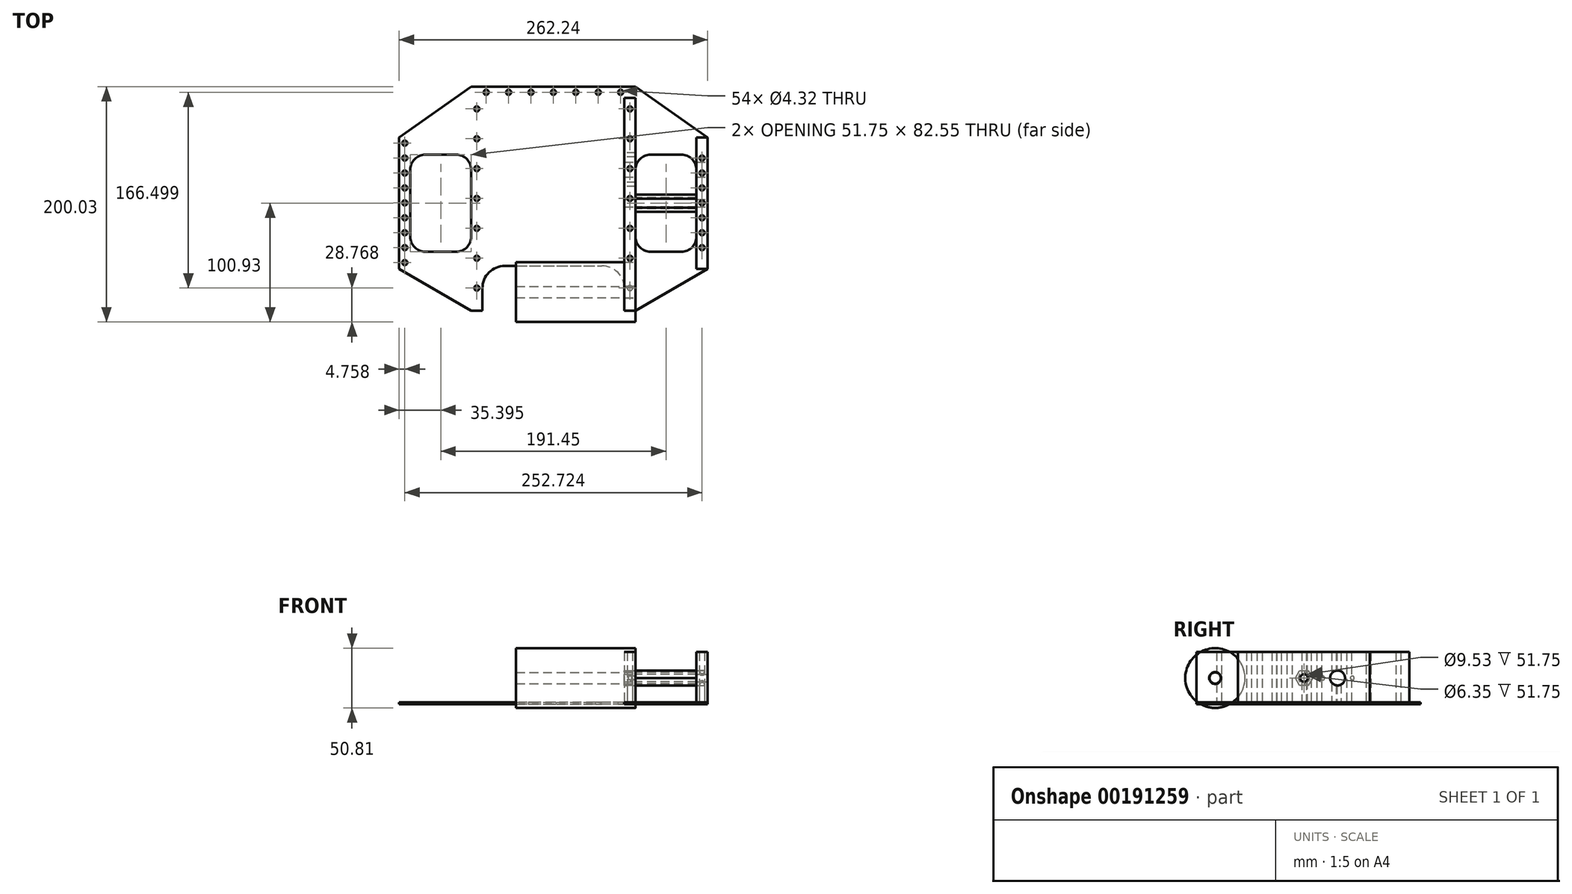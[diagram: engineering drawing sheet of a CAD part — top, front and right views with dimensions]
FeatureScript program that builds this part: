
annotation { "Feature Type Name" : "Feature", "Feature Type Description" : "" }
export const myFeature = defineFeature(function(context is Context, id is Id, definition is map)
    precondition{}
    {
        {
            var Q0;
            Q0=qCreatedBy(makeId("Top.planeOp"),FACE);
            var sketch = newSketch(context, id + "F0", { "sketchPlane" : qUnion([Q0])});
            skLineSegment(sketch, "E0.bottom", {"start": v(82.55, 31.75) * mm, "end": v(114.3, 31.75) * mm});
            skLineSegment(sketch, "E0.top", {"start": v(82.55, -31.75) * mm, "end": v(114.3, -31.75) * mm});
            skLineSegment(sketch, "E0.left", {"start": v(82.55, 31.75) * mm, "end": v(82.55, -31.75) * mm});
            skLineSegment(sketch, "E0.right", {"start": v(114.3, 31.75) * mm, "end": v(114.3, -31.75) * mm});
            skPoint(sketch, "E0.middle", {"position": v(98.43, 0) * mm});
            skLineSegment(sketch, "E1.bottom", {"start": v(48.7, -59.65) * mm, "end": v(-48.7, -59.65) * mm, "construction": true});
            skLineSegment(sketch, "E1.left", {"start": v(48.7, -59.65) * mm, "end": v(48.7, -91.4) * mm, "construction": true});
            skLineSegment(sketch, "E1.right", {"start": v(-48.7, -59.65) * mm, "end": v(-48.7, -91.4) * mm, "construction": true});
            skPoint(sketch, "E1.middle", {"position": v(0, -75.53) * mm});
            skLineSegment(sketch, "E2", {"start": v(0, 0) * mm, "end": v(0, 61.83) * mm, "construction": true});
            skLineSegment(sketch, "E3.MirrorCS", {"start": v(-82.55, 31.75) * mm, "end": v(-114.3, 31.75) * mm});
            skLineSegment(sketch, "E4.MirrorCS", {"start": v(-82.55, -31.75) * mm, "end": v(-114.3, -31.75) * mm});
            skLineSegment(sketch, "E5.MirrorCS", {"start": v(-82.55, 31.75) * mm, "end": v(-82.55, -31.75) * mm});
            skLineSegment(sketch, "E6.MirrorCS", {"start": v(-114.3, 31.75) * mm, "end": v(-114.3, -31.75) * mm});
            skPoint(sketch, "E7.MirrorP", {"position": v(-98.43, 0) * mm});
            skLineSegment(sketch, "E8.bottom", {"start": v(69.85, 89.57) * mm, "end": v(0, 89.57) * mm});
            skLineSegment(sketch, "E8.top", {"start": v(69.85, 99.1) * mm, "end": v(0, 99.1) * mm});
            skPoint(sketch, "E9.middle", {"position": v(80.32, 28.57) * mm});
            skLineSegment(sketch, "E10.bottom", {"start": v(60.33, 7.57) * mm, "end": v(10.32, 7.57) * mm});
            skLineSegment(sketch, "E10.top", {"start": v(60.33, 49.57) * mm, "end": v(10.32, 49.57) * mm});
            skLineSegment(sketch, "E10.left", {"start": v(60.33, 7.57) * mm, "end": v(60.33, 49.57) * mm});
            skLineSegment(sketch, "E10.right", {"start": v(10.32, 7.57) * mm, "end": v(10.32, 49.57) * mm});
            skPoint(sketch, "E10.middle", {"position": v(35.33, 28.57) * mm});
            skLineSegment(sketch, "E11.bottom", {"start": v(60.33, 89.57) * mm, "end": v(69.85, 89.57) * mm});
            skLineSegment(sketch, "E11.top", {"start": v(60.33, -91.4) * mm, "end": v(69.85, -91.4) * mm});
            skLineSegment(sketch, "E11.left", {"start": v(60.33, 89.57) * mm, "end": v(60.33, -91.4) * mm});
            skLineSegment(sketch, "E11.right", {"start": v(69.85, 89.57) * mm, "end": v(69.85, -91.4) * mm});
            skLineSegment(sketch, "E12.bottom", {"start": v(60.33, 31.07) * mm, "end": v(80.32, 31.07) * mm});
            skLineSegment(sketch, "E12.top", {"start": v(60.33, 26.07) * mm, "end": v(80.32, 26.07) * mm});
            skLineSegment(sketch, "E12.left", {"start": v(60.33, 31.07) * mm, "end": v(60.33, 26.07) * mm});
            skLineSegment(sketch, "E12.right", {"start": v(80.32, 31.07) * mm, "end": v(80.32, 26.07) * mm});
            skLineSegment(sketch, "E13.bottom", {"start": v(73.03, 23.81) * mm, "end": v(82.55, 23.81) * mm});
            skLineSegment(sketch, "E13.top", {"start": v(73.03, -23.81) * mm, "end": v(82.55, -23.81) * mm});
            skLineSegment(sketch, "E13.left", {"start": v(73.03, 23.81) * mm, "end": v(73.03, -23.81) * mm});
            skLineSegment(sketch, "E13.right", {"start": v(82.55, 23.81) * mm, "end": v(82.55, -23.81) * mm});
            skPoint(sketch, "E13.middle", {"position": v(77.79, 0) * mm});
            skLineSegment(sketch, "E14.bottom", {"start": v(80.32, 33.34) * mm, "end": v(67.62, 33.34) * mm});
            skLineSegment(sketch, "E14.top", {"start": v(80.32, 23.81) * mm, "end": v(67.62, 23.81) * mm});
            skLineSegment(sketch, "E14.left", {"start": v(80.32, 33.34) * mm, "end": v(80.32, 23.81) * mm});
            skLineSegment(sketch, "E14.right", {"start": v(67.62, 33.34) * mm, "end": v(67.62, 23.81) * mm});
            skPoint(sketch, "E14.middle", {"position": v(73.97, 28.57) * mm});
            skLineSegment(sketch, "E15", {"start": v(69.85, 99.1) * mm, "end": v(69.85, 89.57) * mm});
            skLineSegment(sketch, "E16", {"start": v(69.85, 99.1) * mm, "end": v(131.12, 56.02) * mm});
            skLineSegment(sketch, "E17.trimOffspring", {"start": v(131.12, 56.02) * mm, "end": v(131.12, -56.02) * mm});
            skLineSegment(sketch, "E18", {"start": v(131.12, -56.02) * mm, "end": v(69.85, -91.4) * mm});
            skPoint(sketch, "E19", {"position": v(131.12, 0) * mm});
            skLineSegment(sketch, "E20.0", {"start": v(121.6, -50.52) * mm, "end": v(69.85, -80.4) * mm, "construction": true});
            skLineSegment(sketch, "E20.1", {"start": v(121.6, 51.08) * mm, "end": v(121.6, -50.52) * mm, "construction": true});
            skLineSegment(sketch, "E21.trimOffspring", {"start": v(69.85, 87.46) * mm, "end": v(121.6, 51.08) * mm, "construction": true});
            skLineSegment(sketch, "E22.bottom", {"start": v(51.38, -53.06) * mm, "end": v(30.38, -53.06) * mm});
            skLineSegment(sketch, "E22.top", {"start": v(51.38, -3.06) * mm, "end": v(30.38, -3.06) * mm});
            skLineSegment(sketch, "E22.left", {"start": v(51.38, -53.06) * mm, "end": v(51.38, -3.06) * mm});
            skLineSegment(sketch, "E22.right", {"start": v(30.38, -53.06) * mm, "end": v(30.38, -3.06) * mm});
            skPoint(sketch, "E22.middle", {"position": v(40.88, -28.06) * mm});
            skSolve(sketch);
        }
        {
            var Q0;
            Q0=qCreatedBy(makeId("Top.planeOp"),FACE);
            var sketch = newSketch(context, id + "F1", { "sketchPlane" : qUnion([Q0])});
            skLineSegment(sketch, "E23.0", {"start": v(69.85, 99.1) * mm, "end": v(0, 99.1) * mm});
            skLineSegment(sketch, "E23.1", {"start": v(69.85, 99.1) * mm, "end": v(131.12, 56.02) * mm});
            skLineSegment(sketch, "E23.2", {"start": v(131.12, 56.02) * mm, "end": v(131.12, -56.02) * mm});
            skLineSegment(sketch, "E23.3", {"start": v(131.12, -56.02) * mm, "end": v(69.85, -91.4) * mm});
            skLineSegment(sketch, "E23.4", {"start": v(60.33, -91.4) * mm, "end": v(69.85, -91.4) * mm});
            skLineSegment(sketch, "E23.5", {"start": v(60.33, -53.3) * mm, "end": v(60.33, -91.4) * mm});
            skLineSegment(sketch, "E24", {"start": v(60.33, -53.3) * mm, "end": v(0, -53.3) * mm});
            skPoint(sketch, "E25.orphan", {"position": v(60.33, 89.57) * mm});
            skLineSegment(sketch, "E26.0", {"start": v(0, 0) * mm, "end": v(0, 61.83) * mm, "construction": true});
            skLineSegment(sketch, "E27.MirrorCS", {"start": v(-69.85, 99.1) * mm, "end": v(0, 99.1) * mm});
            skLineSegment(sketch, "E28.MirrorCS", {"start": v(-69.85, 99.1) * mm, "end": v(-131.12, 56.02) * mm});
            skLineSegment(sketch, "E29.MirrorCS", {"start": v(-60.33, -53.3) * mm, "end": v(0, -53.3) * mm});
            skPoint(sketch, "E30.MirrorP", {"position": v(-60.33, 89.57) * mm});
            skLineSegment(sketch, "E31.MirrorCS", {"start": v(-60.33, -53.3) * mm, "end": v(-60.33, -91.4) * mm});
            skLineSegment(sketch, "E32.MirrorCS", {"start": v(-60.33, -91.4) * mm, "end": v(-69.85, -91.4) * mm});
            skLineSegment(sketch, "E33.MirrorCS", {"start": v(-131.12, 56.02) * mm, "end": v(-131.12, -56.02) * mm});
            skLineSegment(sketch, "E34.MirrorCS", {"start": v(-131.12, -56.02) * mm, "end": v(-69.85, -91.4) * mm});
            skSolve(sketch);
        }
        {
            var Q0;
            Q0=qCreatedBy(makeId("Top.planeOp"),FACE);
            var sketch = newSketch(context, id + "F2", { "sketchPlane" : qUnion([Q0])});
            skPoint(sketch, "E35.0", {"position": v(65.09, 89.57) * mm});
            skPoint(sketch, "E35.1", {"position": v(65.09, -91.4) * mm});
            skPoint(sketch, "E36.0", {"position": v(121.6, 51.08) * mm});
            skPoint(sketch, "E36.1", {"position": v(121.6, -50.52) * mm});
            skLineSegment(sketch, "E37", {"start": v(65.09, 89.57) * mm, "end": v(65.09, -91.4) * mm, "construction": true});
            skLineSegment(sketch, "E38.0", {"start": v(131.12, 56.02) * mm, "end": v(131.12, -56.02) * mm, "construction": true});
            skLineSegment(sketch, "E39", {"start": v(121.6, 51.08) * mm, "end": v(131.12, 51.08) * mm, "construction": true});
            skLineSegment(sketch, "E40", {"start": v(126.36, 51.08) * mm, "end": v(126.36, -50.52) * mm, "construction": true});
            skPoint(sketch, "E41.0", {"position": v(69.85, 94.34) * mm});
            skPoint(sketch, "E42.0", {"position": v(0, 99.1) * mm});
            skPoint(sketch, "E42.1", {"position": v(0, 89.57) * mm});
            skLineSegment(sketch, "E43", {"start": v(0, 99.1) * mm, "end": v(0, 89.57) * mm, "construction": true});
            skLineSegment(sketch, "E44", {"start": v(0, 94.34) * mm, "end": v(69.85, 94.34) * mm, "construction": true});
            skPoint(sketch, "E45", {"position": v(126.36, 38.38) * mm});
            skPoint(sketch, "E46.0.1.0", {"position": v(126.36, 25.68) * mm});
            skPoint(sketch, "E46.0.2.0", {"position": v(126.36, 12.98) * mm});
            skPoint(sketch, "E46.0.3.0", {"position": v(126.36, 0.28) * mm});
            skPoint(sketch, "E46.0.4.0", {"position": v(126.36, -12.42) * mm});
            skPoint(sketch, "E46.0.5.0", {"position": v(126.36, -25.12) * mm});
            skPoint(sketch, "E46.0.6.0", {"position": v(126.36, -37.82) * mm});
            skLineSegment(sketch, "E46.direction1", {"start": v(126.36, 38.38) * mm, "end": v(151.76, 38.38) * mm, "construction": true});
            skLineSegment(sketch, "E46.direction2", {"start": v(126.36, 38.38) * mm, "end": v(126.36, 25.68) * mm, "construction": true});
            skPoint(sketch, "E47", {"position": v(65.09, 80.24) * mm});
            skPoint(sketch, "E48.0.1.0", {"position": v(65.09, 54.84) * mm});
            skPoint(sketch, "E48.0.2.0", {"position": v(65.09, 29.44) * mm});
            skPoint(sketch, "E48.0.3.0", {"position": v(65.09, 4.04) * mm});
            skPoint(sketch, "E48.0.4.0", {"position": v(65.09, -21.36) * mm});
            skPoint(sketch, "E48.0.5.0", {"position": v(65.09, -46.76) * mm});
            skPoint(sketch, "E48.0.6.0", {"position": v(65.09, -72.16) * mm});
            skLineSegment(sketch, "E48.direction1", {"start": v(65.09, 80.24) * mm, "end": v(90.49, 80.24) * mm, "construction": true});
            skLineSegment(sketch, "E48.direction2", {"start": v(65.09, 80.24) * mm, "end": v(65.09, 54.84) * mm, "construction": true});
            skPoint(sketch, "E49", {"position": v(57.15, 94.34) * mm});
            skPoint(sketch, "E50.1.0.0", {"position": v(38.1, 94.34) * mm});
            skPoint(sketch, "E50.2.0.0", {"position": v(19.05, 94.34) * mm});
            skLineSegment(sketch, "E50.direction1", {"start": v(57.15, 94.34) * mm, "end": v(38.1, 94.34) * mm, "construction": true});
            skPoint(sketch, "E51.MirrorP", {"position": v(-126.36, -37.82) * mm});
            skLineSegment(sketch, "E52.MirrorCS", {"start": v(-65.09, 80.24) * mm, "end": v(-65.09, 54.84) * mm, "construction": true});
            skPoint(sketch, "E53.MirrorP", {"position": v(-65.09, -46.76) * mm});
            skLineSegment(sketch, "E54.MirrorCS", {"start": v(-126.36, 38.38) * mm, "end": v(-126.36, 25.68) * mm, "construction": true});
            skLineSegment(sketch, "E55.MirrorCS", {"start": v(-65.09, 89.57) * mm, "end": v(-65.09, -91.4) * mm, "construction": true});
            skLineSegment(sketch, "E56.MirrorCS", {"start": v(-126.36, 51.08) * mm, "end": v(-126.36, -50.52) * mm, "construction": true});
            skPoint(sketch, "E57.MirrorP", {"position": v(-19.05, 94.34) * mm});
            skPoint(sketch, "E58.MirrorP", {"position": v(-126.36, -12.42) * mm});
            skPoint(sketch, "E59.MirrorP", {"position": v(-126.36, 38.38) * mm});
            skPoint(sketch, "E60.MirrorP", {"position": v(-65.09, 80.24) * mm});
            skPoint(sketch, "E61.MirrorP", {"position": v(-126.36, 0.28) * mm});
            skPoint(sketch, "E62.MirrorP", {"position": v(-57.15, 94.34) * mm});
            skPoint(sketch, "E63.MirrorP", {"position": v(-126.36, 12.98) * mm});
            skPoint(sketch, "E64.MirrorP", {"position": v(-65.09, 54.84) * mm});
            skPoint(sketch, "E65.MirrorP", {"position": v(-126.36, -25.12) * mm});
            skPoint(sketch, "E66.MirrorP", {"position": v(-65.09, 89.57) * mm});
            skPoint(sketch, "E67.MirrorP", {"position": v(-65.09, 29.44) * mm});
            skPoint(sketch, "E68.MirrorP", {"position": v(-38.1, 94.34) * mm});
            skPoint(sketch, "E69.MirrorP", {"position": v(-65.09, 4.04) * mm});
            skPoint(sketch, "E70.MirrorP", {"position": v(-65.09, -91.4) * mm});
            skPoint(sketch, "E71.MirrorP", {"position": v(-65.09, -72.16) * mm});
            skPoint(sketch, "E72.MirrorP", {"position": v(-69.85, 94.34) * mm});
            skPoint(sketch, "E73.MirrorP", {"position": v(-65.09, -21.36) * mm});
            skPoint(sketch, "E74.MirrorP", {"position": v(-126.36, 25.68) * mm});
            skSolve(sketch);
        }
        {
            var Q0;
            Q0 = qSketchRegion(id + "F1", true);
            extrude(context, id + "F3", {"entities" : qUnion([Q0]), "depth" : 1.52 * mm});
        }
        {
            var Q0;
            Q0=sQuery(id+"F2.wireOp",VERTEX,"E50.2.0.0");
            var Q1;
            Q1=sQuery(id+"F2.wireOp",VERTEX,"E50.1.0.0");
            var Q2;
            Q2=sQuery(id+"F2.wireOp",VERTEX,"E49");
            var Q3;
            Q3=sQuery(id+"F2.wireOp",VERTEX,"E47");
            var Q4;
            Q4=sQuery(id+"F2.wireOp",VERTEX,"E48.0.1.0");
            var Q5;
            Q5=sQuery(id+"F2.wireOp",VERTEX,"E48.0.2.0");
            var Q6;
            Q6=sQuery(id+"F2.wireOp",VERTEX,"E48.0.3.0");
            var Q7;
            Q7=sQuery(id+"F2.wireOp",VERTEX,"E48.0.4.0");
            var Q8;
            Q8=sQuery(id+"F2.wireOp",VERTEX,"E48.0.5.0");
            var Q9;
            Q9=sQuery(id+"F2.wireOp",VERTEX,"E48.0.6.0");
            var Q10;
            Q10=sQuery(id+"F2.wireOp",VERTEX,"E46.0.6.0");
            var Q11;
            Q11=sQuery(id+"F2.wireOp",VERTEX,"E46.0.5.0");
            var Q12;
            Q12=sQuery(id+"F2.wireOp",VERTEX,"E46.0.4.0");
            var Q13;
            Q13=sQuery(id+"F2.wireOp",VERTEX,"E46.0.3.0");
            var Q14;
            Q14=sQuery(id+"F2.wireOp",VERTEX,"E46.0.2.0");
            var Q15;
            Q15=sQuery(id+"F2.wireOp",VERTEX,"E46.0.1.0");
            var Q16;
            Q16=sQuery(id+"F2.wireOp",VERTEX,"E45");
            var Q17;
            Q17=sQuery(id+"F2.wireOp",VERTEX,"E74.MirrorP");
            var Q18;
            Q18=sQuery(id+"F2.wireOp",VERTEX,"E58.MirrorP");
            var Q19;
            Q19=sQuery(id+"F2.wireOp",VERTEX,"E65.MirrorP");
            var Q20;
            Q20=sQuery(id+"F2.wireOp",VERTEX,"E56.MirrorCS.end");
            var Q21;
            Q21=sQuery(id+"F2.wireOp",VERTEX,"E51.MirrorP");
            var Q22;
            Q22=sQuery(id+"F2.wireOp",VERTEX,"E59.MirrorP");
            var Q23;
            Q23=sQuery(id+"F2.wireOp",VERTEX,"E61.MirrorP");
            var Q24;
            Q24=sQuery(id+"F2.wireOp",VERTEX,"E56.MirrorCS.start");
            var Q25;
            Q25=sQuery(id+"F2.wireOp",VERTEX,"E63.MirrorP");
            var Q26;
            Q26=sQuery(id+"F2.wireOp",VERTEX,"E68.MirrorP");
            var Q27;
            Q27=sQuery(id+"F2.wireOp",VERTEX,"E62.MirrorP");
            var Q28;
            Q28=sQuery(id+"F2.wireOp",VERTEX,"E57.MirrorP");
            var Q29;
            Q29=sQuery(id+"F2.wireOp",VERTEX,"E60.MirrorP");
            var Q30;
            Q30=sQuery(id+"F2.wireOp",VERTEX,"E67.MirrorP");
            var Q31;
            Q31=sQuery(id+"F2.wireOp",VERTEX,"E53.MirrorP");
            var Q32;
            Q32=sQuery(id+"F2.wireOp",VERTEX,"E69.MirrorP");
            var Q33;
            Q33=sQuery(id+"F2.wireOp",VERTEX,"E64.MirrorP");
            var Q34;
            Q34=sQuery(id+"F2.wireOp",VERTEX,"E71.MirrorP");
            var Q35;
            Q35=sQuery(id+"F2.wireOp",VERTEX,"E73.MirrorP");
            var Q36;
            Q36=sQuery(id+"F2.wireOp",VERTEX,"E44.start");
            var Q37;
            Q37=makeQuery(id+"F3.opExtrude","SWEPT_BODY",BODY,{"disambiguationData":[OSD([sQuery(id+"F1.wireOp",EDGE,"E23.0"),sQuery(id+"F1.wireOp",EDGE,"E23.1"),sQuery(id+"F1.wireOp",EDGE,"E23.2"),sQuery(id+"F1.wireOp",EDGE,"E23.3"),sQuery(id+"F1.wireOp",EDGE,"E23.4"),sQuery(id+"F1.wireOp",EDGE,"E23.5"),sQuery(id+"F1.wireOp",EDGE,"E24"),sQuery(id+"F1.wireOp",EDGE,"E27.MirrorCS"),sQuery(id+"F1.wireOp",EDGE,"E28.MirrorCS"),sQuery(id+"F1.wireOp",EDGE,"E29.MirrorCS"),sQuery(id+"F1.wireOp",EDGE,"E31.MirrorCS"),sQuery(id+"F1.wireOp",EDGE,"E32.MirrorCS"),sQuery(id+"F1.wireOp",EDGE,"E33.MirrorCS"),sQuery(id+"F1.wireOp",EDGE,"E34.MirrorCS")])]});
            hole(context, id + "F4", {"style" : HoleStyle.SIMPLE, "endStyle" : HoleEndStyle.THROUGH, "oppositeDirection" : true, "standardTappedOrClearance" : lookupTablePath({ "standard" : "ANSI", "fit" : "Close", "size" : "#8", "type" : "Clearance" }), "standardBlindInLast" : lookupTablePath({ "fit" : "Close", "standard" : "ANSI", "size" : "#8", "type" : "Clearance" }), "holeDiameter" : 4.32 * mm, "locations" : qUnion([Q0, Q1, Q2, Q3, Q4, Q5, Q6, Q7, Q8, Q9, Q10, Q11, Q12, Q13, Q14, Q15, Q16, Q17, Q18, Q19, Q20, Q21, Q22, Q23, Q24, Q25, Q26, Q27, Q28, Q29, Q30, Q31, Q32, Q33, Q34, Q35, Q36]), "scope" : qUnion([Q37]), "isTappedThrough" : true});
        }
        {
            var Q0;
            Q0=qCreatedBy(makeId("Top.planeOp"),FACE);
            var sketch = newSketch(context, id + "F5", { "sketchPlane" : qUnion([Q0])});
            skLineSegment(sketch, "E75.0", {"start": v(69.85, 41.28) * mm, "end": v(69.85, -41.27) * mm});
            skLineSegment(sketch, "E75.1", {"start": v(121.6, 41.28) * mm, "end": v(121.6, -41.27) * mm});
            skLineSegment(sketch, "E76", {"start": v(121.6, 41.28) * mm, "end": v(69.85, 41.28) * mm});
            skLineSegment(sketch, "E77", {"start": v(69.85, -41.27) * mm, "end": v(121.6, -41.27) * mm});
            skPoint(sketch, "E78.orphan", {"position": v(69.85, 89.57) * mm});
            skPoint(sketch, "E79.orphan", {"position": v(121.6, 51.08) * mm});
            skPoint(sketch, "E80.orphan", {"position": v(121.6, -50.52) * mm});
            skPoint(sketch, "E81.orphan", {"position": v(69.85, -91.4) * mm});
            skLineSegment(sketch, "E82.MirrorCS", {"start": v(-121.6, 41.28) * mm, "end": v(-121.6, -41.27) * mm});
            skLineSegment(sketch, "E83.MirrorCS", {"start": v(-121.6, 41.28) * mm, "end": v(-69.85, 41.28) * mm});
            skLineSegment(sketch, "E84.MirrorCS", {"start": v(-69.85, -41.27) * mm, "end": v(-121.6, -41.27) * mm});
            skLineSegment(sketch, "E85.MirrorCS", {"start": v(-69.85, 41.28) * mm, "end": v(-69.85, -41.27) * mm});
            skSolve(sketch);
        }
        {
            var Q0;
            Q0 = qSketchRegion(id + "F5", true);
            extrude(context, id + "F6", {"entities" : qUnion([Q0]), "operationType" : NewBodyOperationType.REMOVE, "endBound" : BoundingType.UP_TO_NEXT, "depth" : 25.4 * mm});
        }
        {
            var Q0;
            Q0=makeQuery(id+"F6.boolean.opBoolean","COPY",EDGE,{"derivedFrom":makeQuery(id+"F6.opExtrude","SWEPT_EDGE",EDGE,{"disambiguationData":[OSD([sQuery(id+"F5.wireOp",EDGE,"E83.MirrorCS"),sQuery(id+"F5.wireOp",EDGE,"E85.MirrorCS")])]})});
            var Q1;
            Q1=makeQuery(id+"F6.boolean.opBoolean","COPY",EDGE,{"derivedFrom":makeQuery(id+"F6.opExtrude","SWEPT_EDGE",EDGE,{"disambiguationData":[OSD([sQuery(id+"F5.wireOp",EDGE,"E82.MirrorCS"),sQuery(id+"F5.wireOp",EDGE,"E83.MirrorCS")])]})});
            var Q2;
            Q2=makeQuery(id+"F6.boolean.opBoolean","COPY",EDGE,{"derivedFrom":makeQuery(id+"F6.opExtrude","SWEPT_EDGE",EDGE,{"disambiguationData":[OSD([sQuery(id+"F5.wireOp",EDGE,"E75.0"),sQuery(id+"F5.wireOp",EDGE,"E77")])]})});
            var Q3;
            Q3=makeQuery(id+"F6.boolean.opBoolean","COPY",EDGE,{"derivedFrom":makeQuery(id+"F6.opExtrude","SWEPT_EDGE",EDGE,{"disambiguationData":[OSD([sQuery(id+"F5.wireOp",EDGE,"E82.MirrorCS"),sQuery(id+"F5.wireOp",EDGE,"E84.MirrorCS")])]})});
            var Q4;
            Q4=makeQuery(id+"F6.boolean.opBoolean","COPY",EDGE,{"derivedFrom":makeQuery(id+"F6.opExtrude","SWEPT_EDGE",EDGE,{"disambiguationData":[OSD([sQuery(id+"F5.wireOp",EDGE,"E75.1"),sQuery(id+"F5.wireOp",EDGE,"E77")])]})});
            var Q5;
            Q5=makeQuery(id+"F6.boolean.opBoolean","COPY",EDGE,{"derivedFrom":makeQuery(id+"F6.opExtrude","SWEPT_EDGE",EDGE,{"disambiguationData":[OSD([sQuery(id+"F5.wireOp",EDGE,"E84.MirrorCS"),sQuery(id+"F5.wireOp",EDGE,"E85.MirrorCS")])]})});
            var Q6;
            Q6=makeQuery(id+"F6.boolean.opBoolean","COPY",EDGE,{"derivedFrom":makeQuery(id+"F6.opExtrude","SWEPT_EDGE",EDGE,{"disambiguationData":[OSD([sQuery(id+"F5.wireOp",EDGE,"E75.1"),sQuery(id+"F5.wireOp",EDGE,"E76")])]})});
            var Q7;
            Q7=makeQuery(id+"F6.boolean.opBoolean","COPY",EDGE,{"derivedFrom":makeQuery(id+"F6.opExtrude","SWEPT_EDGE",EDGE,{"disambiguationData":[OSD([sQuery(id+"F5.wireOp",EDGE,"E75.0"),sQuery(id+"F5.wireOp",EDGE,"E76")])]})});
            fillet(context, id + "F7", {"entities" : qUnion([Q0, Q1, Q2, Q3, Q4, Q5, Q6, Q7]), "radius" : 12.7 * mm, "tangentPropagation" : true, "allowEdgeOverflow" : false});
        }
        {
            var Q0;
            Q0=makeQuery(id+"F3.opExtrude","SWEPT_EDGE",EDGE,{"disambiguationData":[OSD([sQuery(id+"F1.wireOp",EDGE,"E29.MirrorCS"),sQuery(id+"F1.wireOp",EDGE,"E31.MirrorCS")])]});
            var Q1;
            Q1=makeQuery(id+"F3.opExtrude","SWEPT_EDGE",EDGE,{"disambiguationData":[OSD([sQuery(id+"F1.wireOp",EDGE,"E23.5"),sQuery(id+"F1.wireOp",EDGE,"E24")])]});
            fillet(context, id + "F8", {"entities" : qUnion([Q0, Q1]), "radius" : 19.05 * mm, "tangentPropagation" : true, "allowEdgeOverflow" : false});
        }
        {
            var Q0;
            Q0=qCreatedBy(makeId("Top.planeOp"),FACE);
            var sketch = newSketch(context, id + "F9", { "sketchPlane" : qUnion([Q0])});
            skLineSegment(sketch, "E86.0", {"start": v(60.33, 89.57) * mm, "end": v(60.33, -91.4) * mm});
            skLineSegment(sketch, "E86.1", {"start": v(60.33, 89.57) * mm, "end": v(69.85, 89.57) * mm});
            skLineSegment(sketch, "E86.2", {"start": v(69.85, 89.57) * mm, "end": v(69.85, -91.4) * mm});
            skLineSegment(sketch, "E86.3", {"start": v(60.33, -91.4) * mm, "end": v(69.85, -91.4) * mm});
            skCircle(sketch, "E87.0", {"center": v(65.09, -72.16) * mm, "radius": 2.16 * mm});
            skCircle(sketch, "E87.1", {"center": v(65.09, -46.76) * mm, "radius": 2.16 * mm});
            skCircle(sketch, "E87.2", {"center": v(65.09, -21.36) * mm, "radius": 2.16 * mm});
            skCircle(sketch, "E87.3", {"center": v(65.09, 4.04) * mm, "radius": 2.16 * mm});
            skCircle(sketch, "E87.4", {"center": v(65.09, 29.44) * mm, "radius": 2.16 * mm});
            skCircle(sketch, "E87.5", {"center": v(65.09, 54.84) * mm, "radius": 2.16 * mm});
            skCircle(sketch, "E87.6", {"center": v(65.09, 80.24) * mm, "radius": 2.16 * mm});
            skLineSegment(sketch, "E88.0", {"start": v(121.6, 56.02) * mm, "end": v(121.6, -56.02) * mm});
            skLineSegment(sketch, "E88.1", {"start": v(131.12, 56.02) * mm, "end": v(131.12, -56.02) * mm});
            skCircle(sketch, "E89.0", {"center": v(126.36, -37.82) * mm, "radius": 2.16 * mm});
            skCircle(sketch, "E89.1", {"center": v(126.36, -25.12) * mm, "radius": 2.16 * mm});
            skCircle(sketch, "E89.2", {"center": v(126.36, -12.42) * mm, "radius": 2.16 * mm});
            skCircle(sketch, "E89.3", {"center": v(126.36, 0.28) * mm, "radius": 2.16 * mm});
            skCircle(sketch, "E89.4", {"center": v(126.36, 12.98) * mm, "radius": 2.16 * mm});
            skCircle(sketch, "E89.5", {"center": v(126.36, 25.68) * mm, "radius": 2.16 * mm});
            skCircle(sketch, "E89.6", {"center": v(126.36, 38.38) * mm, "radius": 2.16 * mm});
            skLineSegment(sketch, "E90", {"start": v(131.12, 56.02) * mm, "end": v(121.6, 56.02) * mm});
            skLineSegment(sketch, "E91", {"start": v(131.12, -56.02) * mm, "end": v(121.6, -56.02) * mm});
            skSolve(sketch);
        }
        {
            var Q0;
            Q0 = qSketchRegion(id + "F9", true);
            extrude(context, id + "F10", {"entities" : qUnion([Q0]), "depth" : 44.45 * mm});
        }
        {
            var Q0;
            Q0=makeQuery(id+"F10.opExtrude","SWEPT_FACE",FACE,{"disambiguationData":[OSD([sQuery(id+"F9.wireOp",EDGE,"E88.1")])]});
            var sketch = newSketch(context, id + "F11", { "sketchPlane" : qUnion([Q0])});
            skPoint(sketch, "E92.0", {"position": v(0, 0) * mm});
            skPoint(sketch, "E92.1", {"position": v(28.57, 0) * mm});
            skCircle(sketch, "E93", {"center": v(0, 22.22) * mm, "radius": 3.18 * mm});
            skCircle(sketch, "E94", {"center": v(28.57, 22.22) * mm, "radius": 6.35 * mm});
            skSolve(sketch);
        }
        {
            var Q0;
            Q0 = qSketchRegion(id + "F11", true);
            var Q1;
            Q1=makeQuery(id+"F10.opExtrude","SWEPT_FACE",FACE,{"disambiguationData":[OSD([sQuery(id+"F9.wireOp",EDGE,"E86.0")])]});
            var Q2;
            Q2=makeQuery(id+"F10.opExtrude","SWEPT_BODY",BODY,{"disambiguationData":[OSD([sQuery(id+"F9.wireOp",EDGE,"E86.0"),sQuery(id+"F9.wireOp",EDGE,"E86.1"),sQuery(id+"F9.wireOp",EDGE,"E86.2"),sQuery(id+"F9.wireOp",EDGE,"E86.3"),sQuery(id+"F9.wireOp",EDGE,"E87.0"),sQuery(id+"F9.wireOp",EDGE,"E87.1"),sQuery(id+"F9.wireOp",EDGE,"E87.2"),sQuery(id+"F9.wireOp",EDGE,"E87.3"),sQuery(id+"F9.wireOp",EDGE,"E87.4"),sQuery(id+"F9.wireOp",EDGE,"E87.5"),sQuery(id+"F9.wireOp",EDGE,"E87.6")])]});
            extrude(context, id + "F12", {"entities" : qUnion([Q0]), "operationType" : NewBodyOperationType.REMOVE, "endBound" : BoundingType.UP_TO_SURFACE, "oppositeDirection" : true, "endBoundEntityFace" : qUnion([Q1]), "endBoundEntityBody" : qUnion([Q2]), "depth" : 25.4 * mm});
        }
        {
            var Q0;
            Q0=makeQuery(id+"F10.opExtrude","SWEPT_FACE",FACE,{"disambiguationData":[OSD([sQuery(id+"F9.wireOp",EDGE,"E86.2")])]});
            var sketch = newSketch(context, id + "F13", { "sketchPlane" : qUnion([Q0])});
            skCircle(sketch, "E95.cCircle", {"center": v(0, 22.22) * mm, "radius": 6.35 * mm, "construction": true});
            skLineSegment(sketch, "E95.0", {"start": v(3.67, 28.57) * mm, "end": v(7.33, 22.22) * mm});
            skLineSegment(sketch, "E95.1", {"start": v(7.33, 22.23) * mm, "end": v(3.67, 15.87) * mm});
            skLineSegment(sketch, "E95.2", {"start": v(3.67, 15.87) * mm, "end": v(-3.67, 15.87) * mm});
            skLineSegment(sketch, "E95.3", {"start": v(-3.67, 15.87) * mm, "end": v(-7.33, 22.22) * mm});
            skLineSegment(sketch, "E95.4", {"start": v(-7.33, 22.22) * mm, "end": v(-3.67, 28.57) * mm});
            skLineSegment(sketch, "E95.5", {"start": v(-3.67, 28.57) * mm, "end": v(3.67, 28.57) * mm});
            skPoint(sketch, "E95.0.midPoint", {"position": v(5.5, 25.4) * mm});
            skCircle(sketch, "E96.0", {"center": v(0, 22.22) * mm, "radius": 4.76 * mm});
            skSolve(sketch);
        }
        {
            var Q0;
            Q0 = qSketchRegion(id + "F13", true);
            extrude(context, id + "F14", {"entities" : qUnion([Q0]), "endBound" : BoundingType.UP_TO_NEXT, "depth" : 25.4 * mm});
        }
        {
            var Q0;
            Q0=makeQuery(id+"F10.opExtrude","SWEPT_FACE",FACE,{"disambiguationData":[OSD([sQuery(id+"F9.wireOp",EDGE,"E86.0")])]});
            var sketch = newSketch(context, id + "F15", { "sketchPlane" : qUnion([Q0])});
            skPoint(sketch, "E97", {"position": v(-16.07, 22.23) * mm});
            skPoint(sketch, "E98.1.0", {"position": v(-41.07, 22.22) * mm});
            skPoint(sketch, "E98.center", {"position": v(-28.57, 22.22) * mm});
            skSolve(sketch);
        }
        {
            var Q0;
            Q0=sQuery(id+"F15.wireOp",VERTEX,"E97");
            var Q1;
            Q1=sQuery(id+"F15.wireOp",VERTEX,"E98.1.0");
            var Q2;
            Q2=makeQuery(id+"F10.opExtrude","SWEPT_BODY",BODY,{"disambiguationData":[OSD([sQuery(id+"F9.wireOp",EDGE,"E86.0"),sQuery(id+"F9.wireOp",EDGE,"E86.1"),sQuery(id+"F9.wireOp",EDGE,"E86.2"),sQuery(id+"F9.wireOp",EDGE,"E86.3"),sQuery(id+"F9.wireOp",EDGE,"E87.0"),sQuery(id+"F9.wireOp",EDGE,"E87.1"),sQuery(id+"F9.wireOp",EDGE,"E87.2"),sQuery(id+"F9.wireOp",EDGE,"E87.3"),sQuery(id+"F9.wireOp",EDGE,"E87.4"),sQuery(id+"F9.wireOp",EDGE,"E87.5"),sQuery(id+"F9.wireOp",EDGE,"E87.6")])]});
            hole(context, id + "F16", {"style" : HoleStyle.SIMPLE, "endStyle" : HoleEndStyle.THROUGH, "standardTappedOrClearance" : lookupTablePath({ "standard" : "ISO", "fit" : "Normal", "size" : "M3", "type" : "Clearance" }), "standardBlindInLast" : lookupTablePath({ "fit" : "Standard", "standard" : "ISO", "size" : "M3", "type" : "Clearance" }), "holeDiameter" : 3.3 * mm, "locations" : qUnion([Q0, Q1]), "scope" : qUnion([Q2]), "isTappedThrough" : true});
        }
        {
            var Q0;
            Q0=makeQuery(id+"F10.opExtrude","SWEPT_FACE",FACE,{"disambiguationData":[OSD([sQuery(id+"F9.wireOp",EDGE,"E86.2")])]});
            var sketch = newSketch(context, id + "F17", { "sketchPlane" : qUnion([Q0])});
            skCircle(sketch, "E99", {"center": v(0, 22.22) * mm, "radius": 4.76 * mm});
            skCircle(sketch, "E100.0", {"center": v(0, 22.22) * mm, "radius": 3.18 * mm});
            skSolve(sketch);
        }
        {
            var Q0;
            Q0=makeQuery(id+"F17.imprint","IMPRINT",FACE,{"disambiguationData":[TD([[makeQuery(id+"F17.imprint","IMPRINT",EDGE,{"derivedFrom":sQuery(id+"F17.wireOp",EDGE,"E99")}),1.0]])]});
            extrude(context, id + "F18", {"entities" : qUnion([Q0]), "endBound" : BoundingType.UP_TO_NEXT, "depth" : 25.4 * mm});
        }
        {
            var Q0;
            Q0=makeQuery(id+"F10.opExtrude","SWEPT_FACE",FACE,{"disambiguationData":[OSD([sQuery(id+"F9.wireOp",EDGE,"E86.2")])]});
            var sketch = newSketch(context, id + "F19", { "sketchPlane" : qUnion([Q0])});
            skCircle(sketch, "E101", {"center": v(-75.53, 22.23) * mm, "radius": 4.76 * mm});
            skCircle(sketch, "E102", {"center": v(-75.53, 22.23) * mm, "radius": 25.4 * mm});
            skSolve(sketch);
        }
        {
            var Q0;
            Q0 = qSketchRegion(id + "F19", true);
            var Q1;
            Q1 = qConstructionFilter(qBodyType(qCreatedBy(id + "F19" ,EDGE), BodyType.WIRE), ConstructionObject.NO);
            extrude(context, id + "F20", {"entities" : qUnion([Q0]), "surfaceEntities" : qUnion([Q1]), "oppositeDirection" : true, "depth" : 101.6 * mm});
        }
        {
            var Q0;
            Q0=sQuery(id+"F19.wireOp",VERTEX,"E102.center");
            var Q1;
            Q1=makeQuery(id+"F10.opExtrude","SWEPT_BODY",BODY,{"disambiguationData":[OSD([sQuery(id+"F9.wireOp",EDGE,"E86.0"),sQuery(id+"F9.wireOp",EDGE,"E86.1"),sQuery(id+"F9.wireOp",EDGE,"E86.2"),sQuery(id+"F9.wireOp",EDGE,"E86.3"),sQuery(id+"F9.wireOp",EDGE,"E87.0"),sQuery(id+"F9.wireOp",EDGE,"E87.1"),sQuery(id+"F9.wireOp",EDGE,"E87.2"),sQuery(id+"F9.wireOp",EDGE,"E87.3"),sQuery(id+"F9.wireOp",EDGE,"E87.4"),sQuery(id+"F9.wireOp",EDGE,"E87.5"),sQuery(id+"F9.wireOp",EDGE,"E87.6")])]});
            hole(context, id + "F21", {"style" : HoleStyle.SIMPLE, "endStyle" : HoleEndStyle.THROUGH, "standardTappedOrClearance" : lookupTablePath({ "standard" : "ANSI", "fit" : "Normal (ASME)", "size" : "3/8", "type" : "Clearance" }), "standardBlindInLast" : lookupTablePath({ "fit" : "Free", "standard" : "ANSI", "size" : "3/8", "type" : "Clearance" }), "holeDiameter" : 10.08 * mm, "locations" : qUnion([Q0]), "scope" : qUnion([Q1]), "isTappedThrough" : true});
        }
    });
